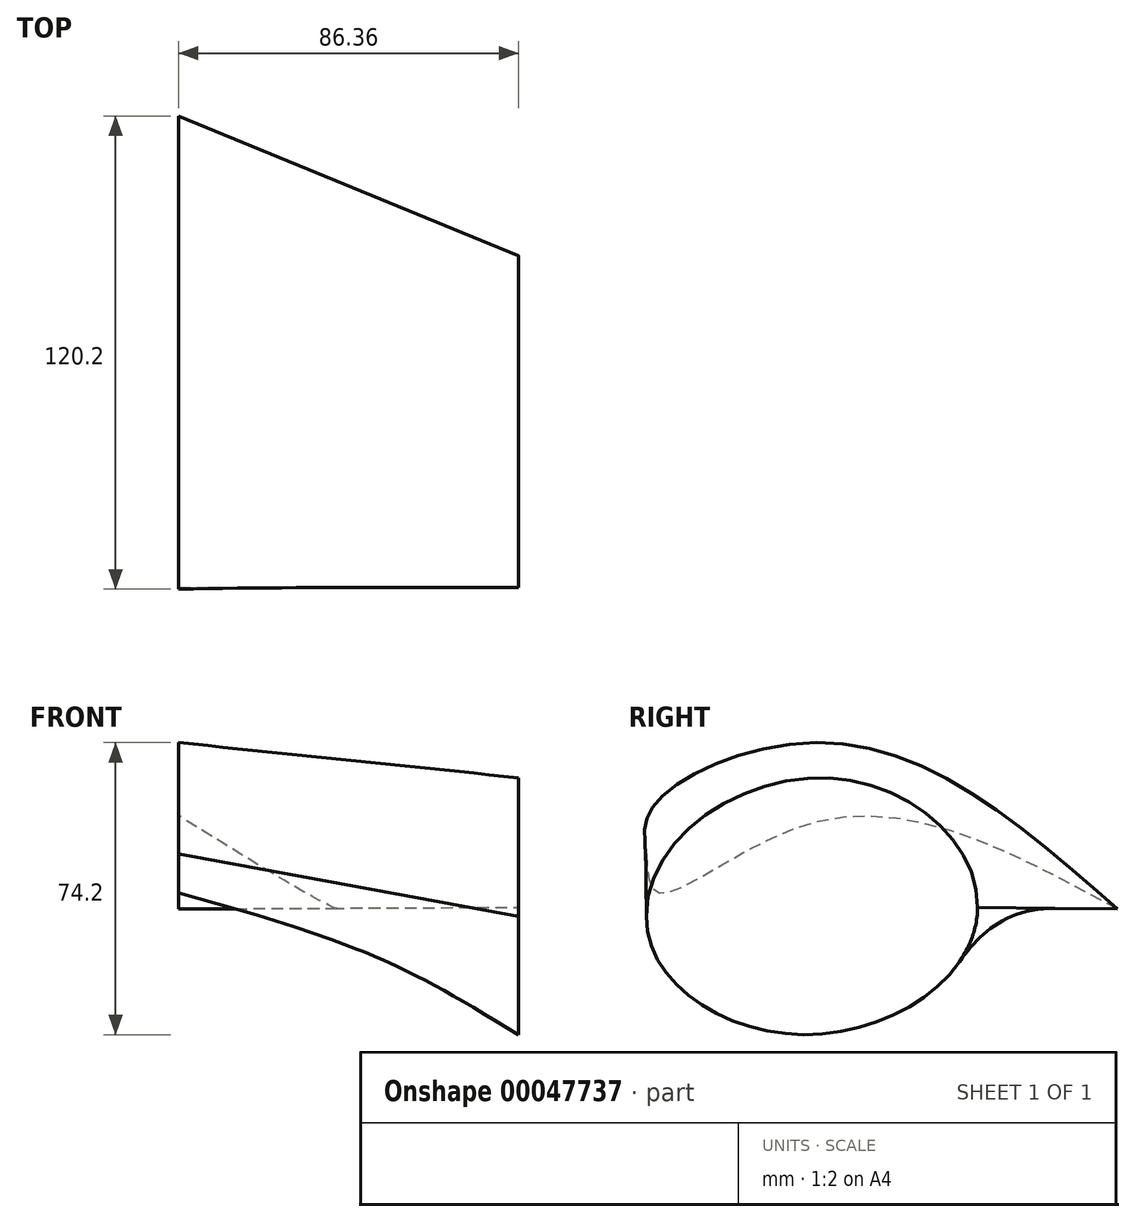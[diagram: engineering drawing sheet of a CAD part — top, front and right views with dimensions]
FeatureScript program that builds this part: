
annotation { "Feature Type Name" : "Feature", "Feature Type Description" : "" }
export const myFeature = defineFeature(function(context is Context, id is Id, definition is map)
    precondition{}
    {
        {
            var Q0;
            Q0=qCreatedBy(makeId("Right.planeOp"),FACE);
            var sketch = newSketch(context, id + "F0", { "sketchPlane" : qUnion([Q0])});
            skFitSpline(sketch, "E0", {"points": [v(0, 0) * mm, v(3.24, -9.83) * mm, v(44.23, 8.47) * mm, v(119.75, -14) * mm], "startDerivative": vector(3.82, -80.18) * mm, "endDerivative": vector(163.73, -89.24) * mm});
            skFitSpline(sketch, "E1", {"points": [v(0, 0) * mm, v(2.04, 12.44) * mm, v(48.96, 28.08) * mm, v(119.75, -14) * mm], "startDerivative": vector(-9.48, 68.1) * mm, "endDerivative": vector(148, -129.55) * mm});
            skSolve(sketch);
        }
        {
            var Q0;
            Q0=qCreatedBy(makeId("Right.planeOp"),FACE);
            cPlane(context, id + "F1", {"entities" : qUnion([Q0]), "cplaneType" : CPlaneType.OFFSET, "offset" : 86.36 * mm, "width" : 152.4 * mm, "height" : 152.4 * mm});
        }
        {
            var Q0;
            Q0=qCreatedBy(id+"F1.planeOp",FACE);
            var sketch = newSketch(context, id + "F2", { "sketchPlane" : qUnion([Q0])});
            skFitSpline(sketch, "E2", {"points": [v(0, -15.88) * mm, v(40.5, -45.9) * mm, v(84.2, -13.55) * mm], "startDerivative": vector(0, -104.37) * mm, "endDerivative": vector(1.5, 107.96) * mm});
            skFitSpline(sketch, "E3", {"points": [v(84.2, -13.55) * mm, v(45.98, 19.33) * mm, v(0, -15.88) * mm], "startDerivative": vector(0.13, 106.23) * mm, "endDerivative": vector(0, -119.36) * mm});
            skSolve(sketch);
        }
        {
            var Q0;
            Q0=makeQuery(id+"F0.imprint","IMPRINT",FACE,{"disambiguationData":[TD([[makeQuery(id+"F0.imprint","IMPRINT",EDGE,{"derivedFrom":sQuery(id+"F0.wireOp",EDGE,"E0")}),1.0]])]});
            var Q1;
            Q1=makeQuery(id+"F2.imprint","IMPRINT",FACE,{"disambiguationData":[TD([[makeQuery(id+"F2.imprint","IMPRINT",EDGE,{"derivedFrom":sQuery(id+"F2.wireOp",EDGE,"E2")}),1.0]])]});
            loft(context, id + "F3", {"sheetProfilesArray" : [{ "sheetProfileEntities" : qUnion([Q0]) }, { "sheetProfileEntities" : qUnion([Q1]) }]});
        }
    });
